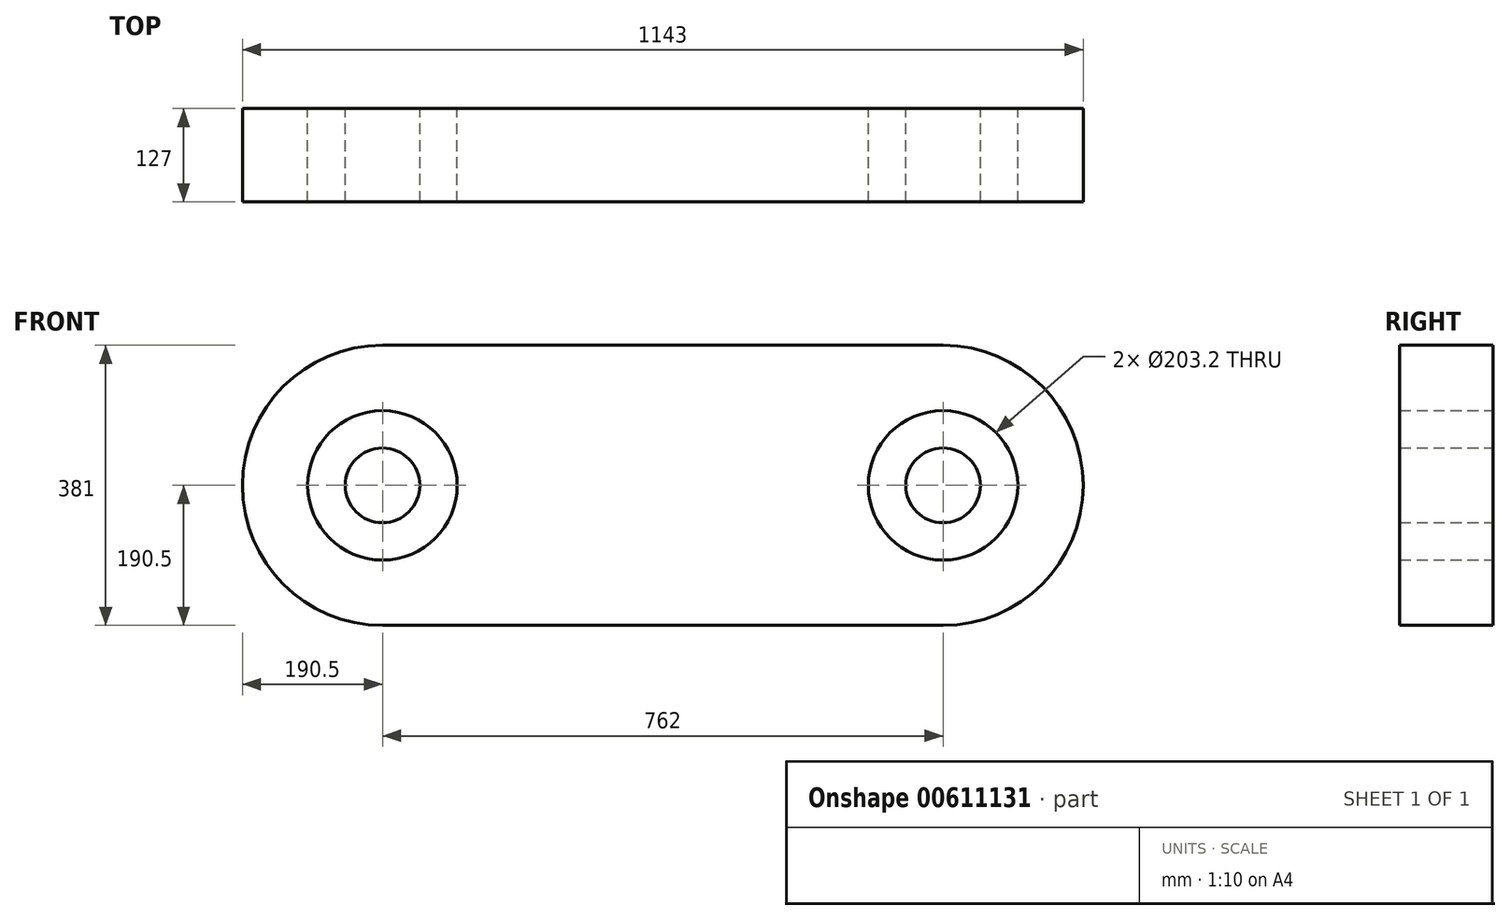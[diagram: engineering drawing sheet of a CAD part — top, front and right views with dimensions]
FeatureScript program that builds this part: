
annotation { "Feature Type Name" : "Feature", "Feature Type Description" : "" }
export const myFeature = defineFeature(function(context is Context, id is Id, definition is map)
    precondition{}
    {
        {
            var Q0;
            Q0=qCreatedBy(makeId("Front.planeOp"),FACE);
            var sketch = newSketch(context, id + "F0", { "sketchPlane" : qUnion([Q0])});
            skLineSegment(sketch, "E0.bottom", {"start": v(381, 190.5) * mm, "end": v(-381, 190.5) * mm});
            skLineSegment(sketch, "E0.top", {"start": v(381, -190.5) * mm, "end": v(-381, -190.5) * mm});
            skPoint(sketch, "E0.middle", {"position": v(0, 0) * mm});
            skArc(sketch, "E1", {"start": v(-381, 190.5) * mm, "mid": v(-571.5, 0) * mm, "end": v(-381, -190.5) * mm});
            skArc(sketch, "E2", {"start": v(381, -190.5) * mm, "mid": v(571.5, 0) * mm, "end": v(381, 190.5) * mm});
            skCircle(sketch, "E3", {"center": v(-381, 0) * mm, "radius": 101.6 * mm});
            skCircle(sketch, "E4", {"center": v(381, 0) * mm, "radius": 101.6 * mm});
            skCircle(sketch, "E5", {"center": v(-381, 0) * mm, "radius": 50.8 * mm});
            skCircle(sketch, "E6", {"center": v(381, 0) * mm, "radius": 50.8 * mm});
            skSolve(sketch);
        }
        {
            var Q0;
            Q0=makeQuery(id+"F0.imprint","IMPRINT",FACE,{"disambiguationData":[TD([[makeQuery(id+"F0.imprint","IMPRINT",EDGE,{"derivedFrom":sQuery(id+"F0.wireOp",EDGE,"E0.bottom")}),1.0]])]});
            var Q1;
            Q1=makeQuery(id+"F0.imprint","IMPRINT",FACE,{"disambiguationData":[TD([[makeQuery(id+"F0.imprint","IMPRINT",EDGE,{"derivedFrom":sQuery(id+"F0.wireOp",EDGE,"E5")}),1.0]])]});
            var Q2;
            Q2=makeQuery(id+"F0.imprint","IMPRINT",FACE,{"disambiguationData":[TD([[makeQuery(id+"F0.imprint","IMPRINT",EDGE,{"derivedFrom":sQuery(id+"F0.wireOp",EDGE,"E6")}),1.0]])]});
            extrude(context, id + "F1", {"entities" : qUnion([Q0, Q1, Q2]), "endBound" : BoundingType.SYMMETRIC, "depth" : 127 * mm, "offsetDistance" : 25.4 * mm});
        }
    });
